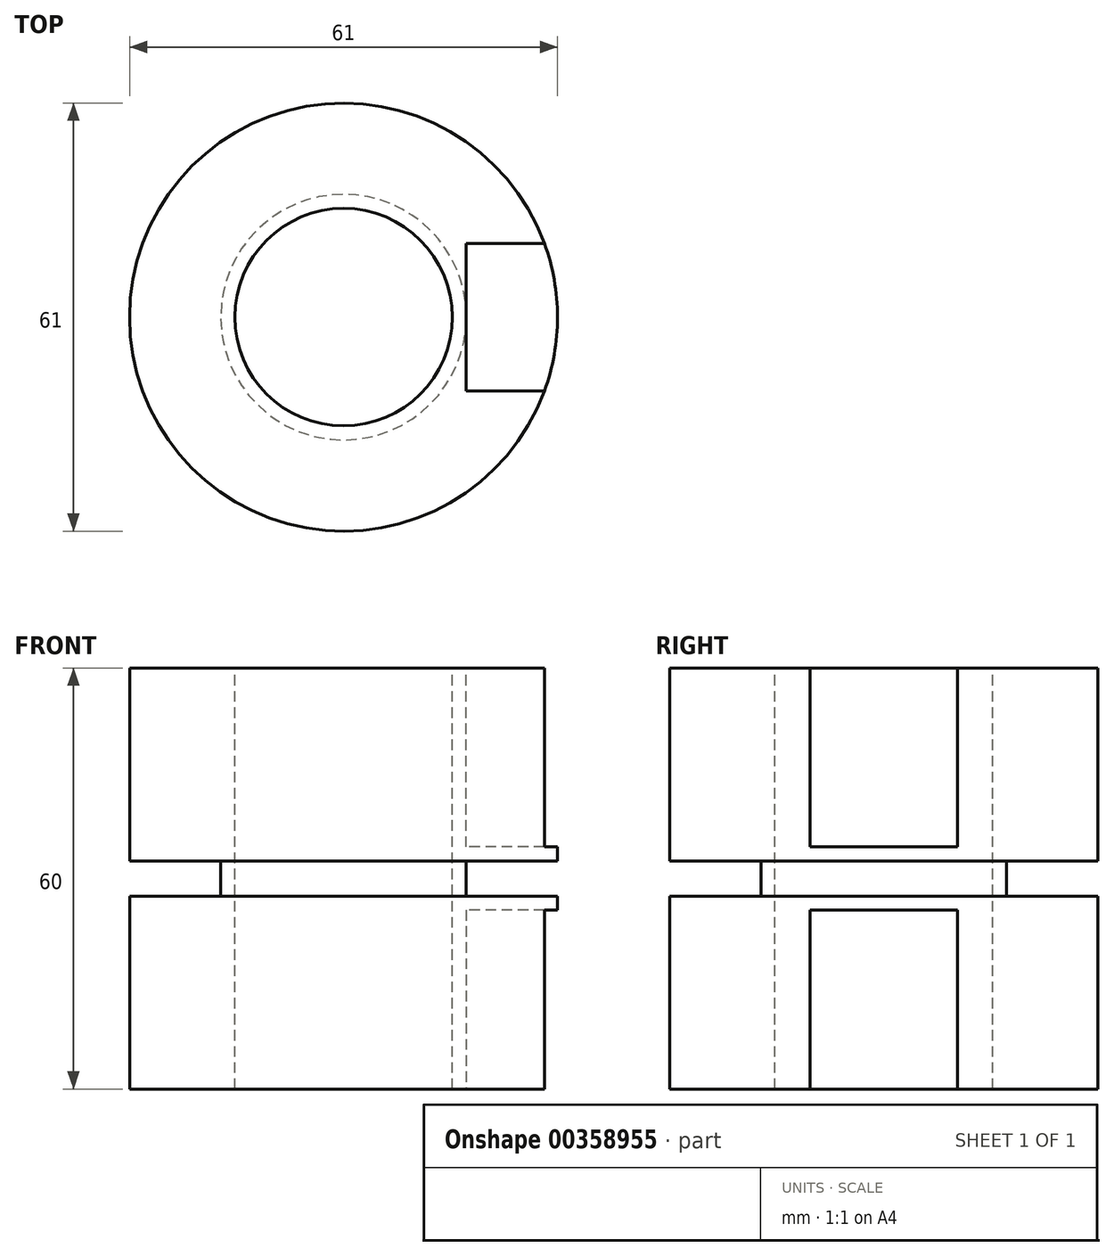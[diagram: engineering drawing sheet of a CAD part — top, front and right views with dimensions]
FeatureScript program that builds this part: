
annotation { "Feature Type Name" : "Feature", "Feature Type Description" : "" }
export const myFeature = defineFeature(function(context is Context, id is Id, definition is map)
    precondition{}
    {
        {
            assignVariable(context, id + "F0", {"variableType" : VariableType.LENGTH, "name" : "Wall_t", "lengthValue" : 2 * mm});
        }
        {
            assignVariable(context, id + "F1", {"variableType" : VariableType.LENGTH, "name" : "Pipe_d", "lengthValue" : 31 * mm});
        }
        {
            var Q0;
            Q0=qCreatedBy(makeId("Front.planeOp"),FACE);
            var sketch = newSketch(context, id + "F2", { "sketchPlane" : qUnion([Q0])});
            skLineSegment(sketch, "E0", {"start": v(15.5, 0) * mm, "end": v(15.5, 30) * mm});
            skLineSegment(sketch, "E1", {"start": v(15.5, 30) * mm, "end": v(30.5, 30) * mm});
            skLineSegment(sketch, "E2", {"start": v(30.5, 30) * mm, "end": v(30.5, 2.5) * mm});
            skLineSegment(sketch, "E3", {"start": v(30.5, 2.5) * mm, "end": v(17.5, 2.5) * mm});
            skLineSegment(sketch, "E4", {"start": v(17.5, 2.5) * mm, "end": v(17.5, 0) * mm});
            skLineSegment(sketch, "E5", {"start": v(17.5, 0) * mm, "end": v(15.5, 0) * mm});
            skLineSegment(sketch, "E6", {"start": v(0, 52.5) * mm, "end": v(0, -39.53) * mm, "construction": true});
            skLineSegment(sketch, "E7", {"start": v(-35.56, 0) * mm, "end": v(50.16, 0) * mm, "construction": true});
            skSolve(sketch);
        }
        {
            var Q0;
            Q0=qCreatedBy(makeId("Right.planeOp"),FACE);
            cPlane(context, id + "F3", {"entities" : qUnion([Q0]), "cplaneType" : CPlaneType.OFFSET, "offset" : getVariable(context, 'Pipe_d') / 2 + getVariable(context, 'Wall_t'), "width" : 150 * mm, "height" : 150 * mm});
        }
        {
            var Q0;
            Q0=qCreatedBy(id+"F3.planeOp",FACE);
            var sketch = newSketch(context, id + "F4", { "sketchPlane" : qUnion([Q0])});
            skLineSegment(sketch, "E8.bottom", {"start": v(10.5, 4.5) * mm, "end": v(-10.5, 4.5) * mm});
            skLineSegment(sketch, "E8.top", {"start": v(10.5, 30) * mm, "end": v(-10.5, 30) * mm});
            skLineSegment(sketch, "E8.left", {"start": v(10.5, 4.5) * mm, "end": v(10.5, 30) * mm});
            skLineSegment(sketch, "E8.right", {"start": v(-10.5, 4.5) * mm, "end": v(-10.5, 30) * mm});
            skPoint(sketch, "E8.middle", {"position": v(0, 17.25) * mm});
            skSolve(sketch);
        }
        {
            var Q0;
            Q0=makeQuery(id+"F2.imprint","IMPRINT",FACE,{"disambiguationData":[TD([[makeQuery(id+"F2.imprint","IMPRINT",EDGE,{"derivedFrom":sQuery(id+"F2.wireOp",EDGE,"E0")}),-1.0]])]});
            var Q1;
            Q1=sQuery(id+"F2.wireOp",EDGE,"E6");
            revolve(context, id + "F5", {"surfaceOperationType" : NewSurfaceOperationType.NEW, "entities" : qUnion([Q0]), "axis" : qUnion([Q1]), "revolveType" : RevolveType.FULL});
        }
        {
            var Q0;
            Q0=makeQuery(id+"F4.imprint","IMPRINT",FACE,{"disambiguationData":[TD([[makeQuery(id+"F4.imprint","IMPRINT",EDGE,{"derivedFrom":sQuery(id+"F4.wireOp",EDGE,"E8.bottom")}),-1.0]])]});
            extrude(context, id + "F6", {"entities" : qUnion([Q0]), "operationType" : NewBodyOperationType.REMOVE, "endBound" : BoundingType.THROUGH_ALL, "depth" : 25 * mm, "offsetDistance" : 25 * mm});
        }
        {
            var Q0;
            Q0=makeQuery(id+"F5.opRevolve","SWEPT_BODY",BODY,{"disambiguationData":[OSD([sQuery(id+"F2.wireOp",EDGE,"E0"),sQuery(id+"F2.wireOp",EDGE,"E1"),sQuery(id+"F2.wireOp",EDGE,"E2"),sQuery(id+"F2.wireOp",EDGE,"E3"),sQuery(id+"F2.wireOp",EDGE,"E4"),sQuery(id+"F2.wireOp",EDGE,"E5")])]});
            var Q1;
            Q1=qCreatedBy(makeId("Top.planeOp"),FACE);
            mirror(context, id + "F7", {"operationType" : NewBodyOperationType.ADD, "entities" : qUnion([Q0]), "mirrorPlane" : qUnion([Q1])});
        }
    });
